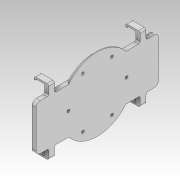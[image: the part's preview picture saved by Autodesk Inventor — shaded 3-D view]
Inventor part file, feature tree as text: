
AUTODESK INVENTOR PART (.ipt)
format: ipt  version: 2020 (Build 240168000, 168)  size: 254,464 bytes
history: native  units: mm
features: sketch x6, extrude x5, fillet x3, projected_geometry x2, revolve x1, plane x1, pattern_circular x1
ambient origin geometry x8: Origin, YZ Plane, XZ Plane, XY Plane, X Axis, Y Axis, Z Axis, Center Point
bodies: Solid1 (feature_tree)
feature tree (19):
  revolve  "Revolution1"  [1 undecoded]
  extrude  "Extrusion1"  Depth=3.3mm
  plane  "Work Plane1"
  extrude  "Extrusion2"  TaperAngle=0.0deg  [1 undecoded]
  pattern_circular  "Circular Pattern1"  Count=6 Angle=360.0deg
  extrude  "Extrusion3"  Depth=2.0mm
  extrude  "Extrusion4"  TaperAngle=45.0deg  [1 undecoded]
  extrude  "Extrusion5"  Depth=2.0mm
  fillet  "Fillet1"  Radius=55.0mm
  fillet  "Fillet2"  Radius=15.0mm
  fillet  "Fillet3"  Radius=7.0mm
  sketch  "Sketch1"  dims[d0=44.0mm d3=1.0mm]
  sketch  "Sketch2"  dims[d6=90.0deg d7=3.3mm]
  sketch  "Sketch3"  dims[d8=35.0mm d9=0.0mm d10=0.0mm]
  sketch  "Sketch4"  dims[d11=-2.0mm]
  sketch  "Sketch5"  dims[d12=6.0mm]
  sketch  "Sketch6"  dims[d13=2.0mm d14=0.0mm d15=60.0mm d16=360.0deg d19=5.0mm d20=45.0deg d21=147.0mm d22=55.0mm d23=15.0mm d24=7.0mm d26=15.0mm d27=10.0mm d28=0.0mm d29=75.0mm d30=2.0mm d31=10.6mm d32=2.0mm d33=1.5mm d34=10.0mm d35=0.0mm d36=10.0mm d37=0.0mm d38=5.0mm d39=2.0mm d40=2.0mm]
  projected_geometry  "Projected Loop1"
  projected_geometry  "Projected Loop2"
note: 3 required parameter values undecoded (feature->parameter linkage not recoverable at this tier; creation-order binding heuristic only, values carry confidence <= 0.55)